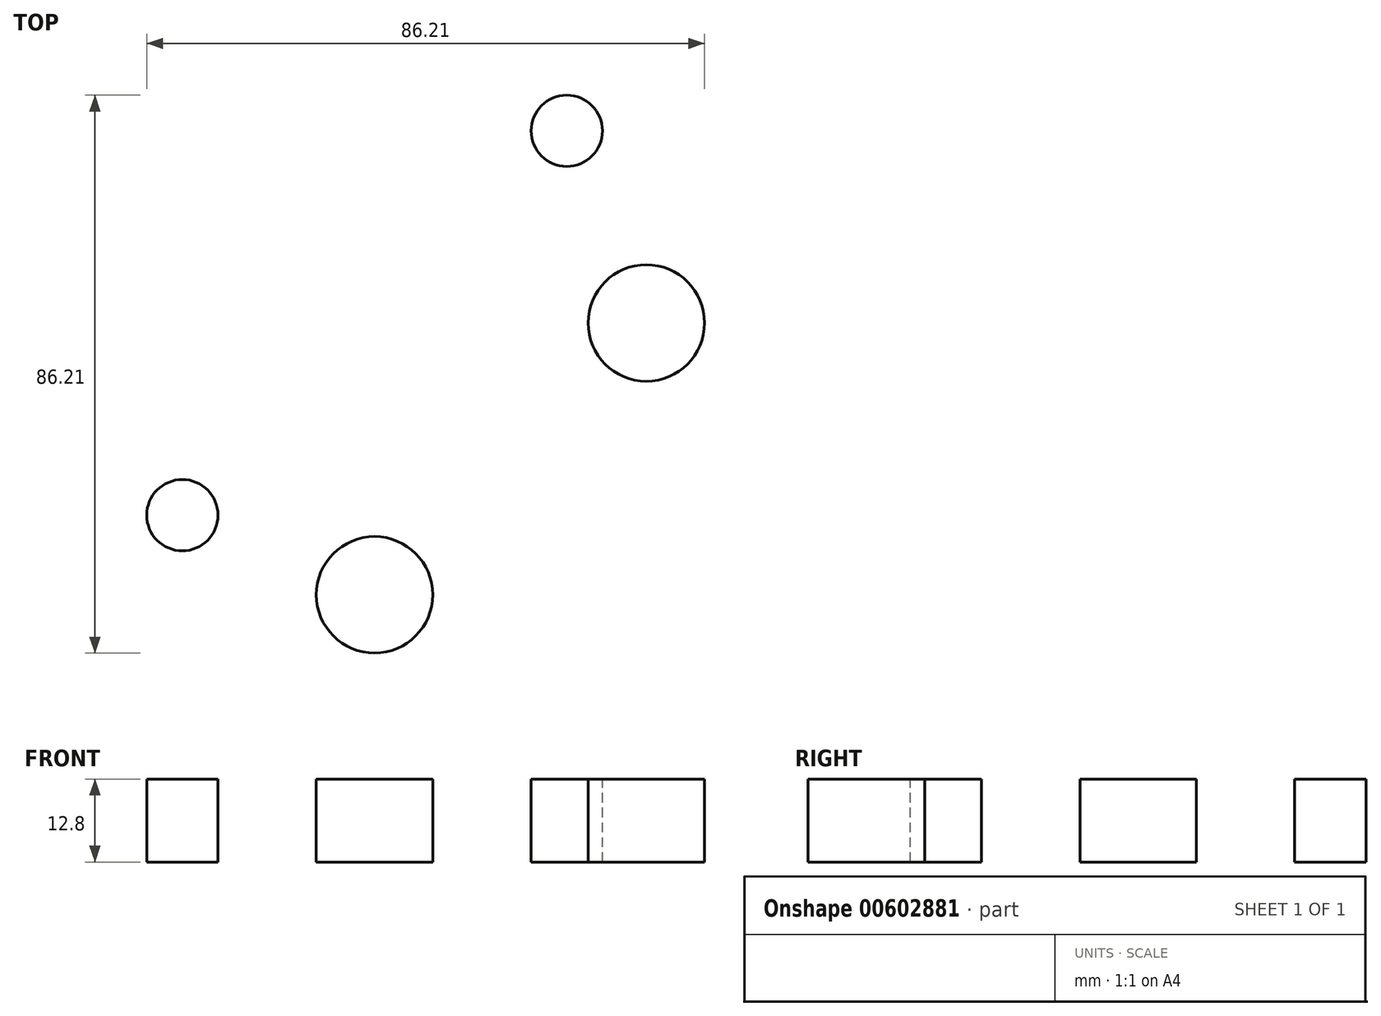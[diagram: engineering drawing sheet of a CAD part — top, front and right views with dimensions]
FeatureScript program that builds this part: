
annotation { "Feature Type Name" : "Feature", "Feature Type Description" : "" }
export const myFeature = defineFeature(function(context is Context, id is Id, definition is map)
    precondition{}
    {
        {
            var Q0;
            Q0=qCreatedBy(makeId("Top.planeOp"),FACE);
            var sketch = newSketch(context, id + "F0", { "sketchPlane" : qUnion([Q0])});
            skCircle(sketch, "E0", {"center": v(0, 0) * mm, "radius": 58 * mm});
            skSolve(sketch);
        }
        {
            var Q0;
            Q0=makeQuery(id+"F0.imprint","IMPRINT",FACE,{"disambiguationData":[TD([[makeQuery(id+"F0.imprint","IMPRINT",EDGE,{"derivedFrom":sQuery(id+"F0.wireOp",EDGE,"E0")}),1.0]])]});
            extrude(context, id + "F1", {"entities" : qUnion([Q0]), "oppositeDirection" : true, "depth" : 12.8 * mm, "offsetDistance" : 25 * mm});
        }
        {
            var Q0;
            Q0=makeQuery(id+"F1.opExtrude","CAP_FACE",FACE,{"disambiguationData":[OSD([sQuery(id+"F0.wireOp",EDGE,"E0")])],"isStart":true});
            var sketch = newSketch(context, id + "F2", { "sketchPlane" : qUnion([Q0])});
            skCircle(sketch, "E1", {"center": v(0, 0) * mm, "radius": 20 * mm});
            skCircle(sketch, "E2", {"center": v(0, 0) * mm, "radius": 25 * mm});
            skSolve(sketch);
        }
        {
            var Q0;
            Q0=makeQuery(id+"F2.imprint","IMPRINT",FACE,{"disambiguationData":[TD([[makeQuery(id+"F2.imprint","IMPRINT",EDGE,{"derivedFrom":sQuery(id+"F2.wireOp",EDGE,"E1")}),1.0]])]});
            extrude(context, id + "F3", {"entities" : qUnion([Q0]), "operationType" : NewBodyOperationType.REMOVE, "oppositeDirection" : true, "depth" : 14.3 * mm, "offsetDistance" : 25 * mm});
        }
        {
            var Q0;
            Q0=makeQuery(id+"F0.imprint","IMPRINT",FACE,{"disambiguationData":[TD([[makeQuery(id+"F0.imprint","IMPRINT",EDGE,{"derivedFrom":sQuery(id+"F0.wireOp",EDGE,"E0")}),1.0]])]});
            var sketch = newSketch(context, id + "F4", { "sketchPlane" : qUnion([Q0])});
            skCircle(sketch, "E3", {"center": v(0, 42) * mm, "radius": 9 * mm});
            skCircle(sketch, "E4", {"center": v(-42, 0) * mm, "radius": 9 * mm});
            skCircle(sketch, "E5.MirrorC", {"center": v(42, 0) * mm, "radius": 9 * mm});
            skCircle(sketch, "E6.MirrorC", {"center": v(0, -42) * mm, "radius": 9 * mm});
            skCircle(sketch, "E7", {"center": v(-29.7, 29.7) * mm, "radius": 5.51 * mm});
            skCircle(sketch, "E8.MirrorC", {"center": v(-29.7, -29.7) * mm, "radius": 5.51 * mm});
            skCircle(sketch, "E9.MirrorC", {"center": v(29.7, -29.7) * mm, "radius": 5.51 * mm});
            skCircle(sketch, "E10.MirrorC", {"center": v(29.7, 29.7) * mm, "radius": 5.51 * mm});
            skSolve(sketch);
        }
        {
            var Q0;
            Q0=makeQuery(id+"F4.imprint","IMPRINT",FACE,{"disambiguationData":[TD([[makeQuery(id+"F4.imprint","IMPRINT",EDGE,{"derivedFrom":sQuery(id+"F4.wireOp",EDGE,"E4")}),1.0]])]});
            var Q1;
            Q1=makeQuery(id+"F4.imprint","IMPRINT",FACE,{"disambiguationData":[TD([[makeQuery(id+"F4.imprint","IMPRINT",EDGE,{"derivedFrom":sQuery(id+"F4.wireOp",EDGE,"E7")}),1.0]])]});
            var Q2;
            Q2=makeQuery(id+"F4.imprint","IMPRINT",FACE,{"disambiguationData":[TD([[makeQuery(id+"F4.imprint","IMPRINT",EDGE,{"derivedFrom":sQuery(id+"F4.wireOp",EDGE,"E8.MirrorC")}),-1.0]])]});
            var Q3;
            Q3=makeQuery(id+"F4.imprint","IMPRINT",FACE,{"disambiguationData":[TD([[makeQuery(id+"F4.imprint","IMPRINT",EDGE,{"derivedFrom":sQuery(id+"F4.wireOp",EDGE,"E6.MirrorC")}),-1.0]])]});
            var Q4;
            Q4=makeQuery(id+"F4.imprint","IMPRINT",FACE,{"disambiguationData":[TD([[makeQuery(id+"F4.imprint","IMPRINT",EDGE,{"derivedFrom":sQuery(id+"F4.wireOp",EDGE,"E10.MirrorC")}),-1.0]])]});
            var Q5;
            Q5=makeQuery(id+"F4.imprint","IMPRINT",FACE,{"disambiguationData":[TD([[makeQuery(id+"F4.imprint","IMPRINT",EDGE,{"derivedFrom":sQuery(id+"F4.wireOp",EDGE,"E5.MirrorC")}),-1.0]])]});
            var Q6;
            Q6=makeQuery(id+"F4.imprint","IMPRINT",FACE,{"disambiguationData":[TD([[makeQuery(id+"F4.imprint","IMPRINT",EDGE,{"derivedFrom":sQuery(id+"F4.wireOp",EDGE,"E9.MirrorC")}),1.0]])]});
            var Q7;
            Q7=makeQuery(id+"F4.imprint","IMPRINT",FACE,{"disambiguationData":[TD([[makeQuery(id+"F4.imprint","IMPRINT",EDGE,{"derivedFrom":sQuery(id+"F4.wireOp",EDGE,"E3")}),1.0]])]});
            extrude(context, id + "F5", {"entities" : qUnion([Q0, Q1, Q2, Q3, Q4, Q5, Q6, Q7]), "operationType" : NewBodyOperationType.REMOVE, "oppositeDirection" : true, "depth" : 25 * mm, "offsetDistance" : 25 * mm});
        }
    });
